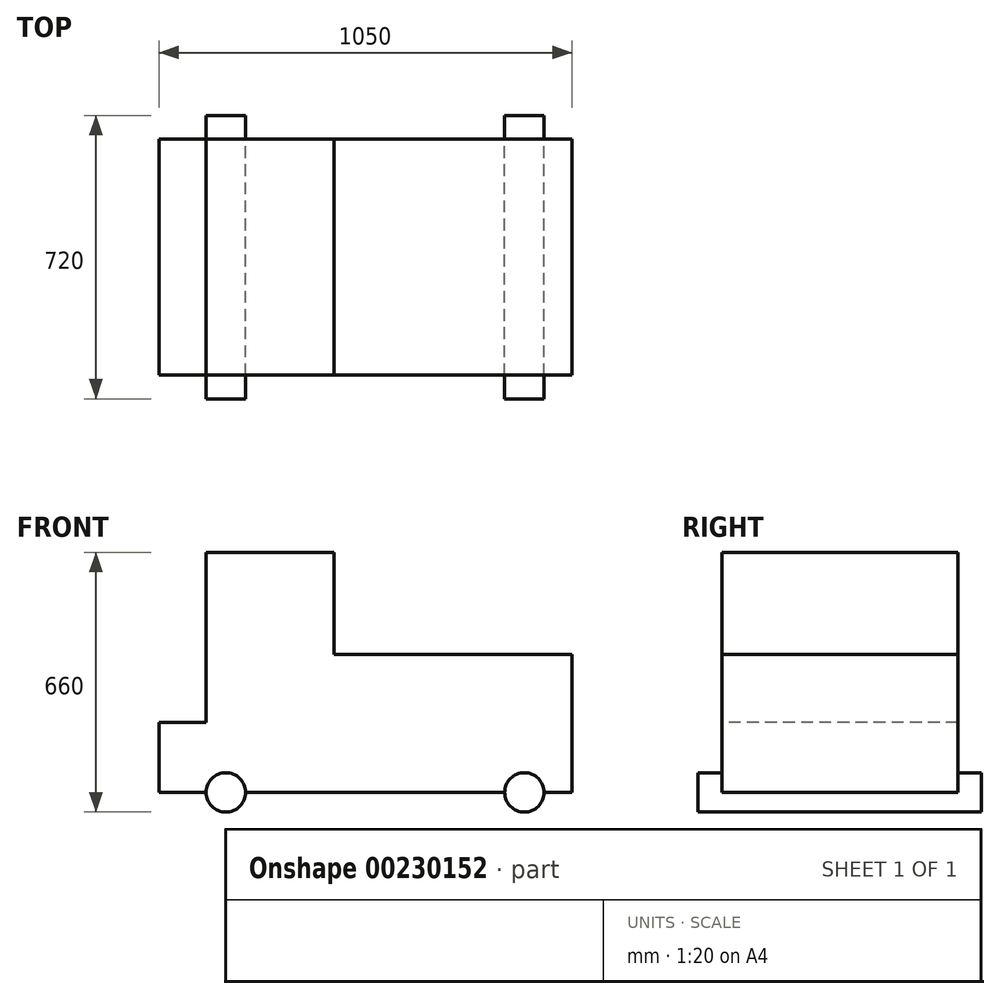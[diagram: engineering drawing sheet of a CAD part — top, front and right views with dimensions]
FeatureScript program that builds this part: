
annotation { "Feature Type Name" : "Feature", "Feature Type Description" : "" }
export const myFeature = defineFeature(function(context is Context, id is Id, definition is map)
    precondition{}
    {
        {
            var Q0;
            Q0=qCreatedBy(makeId("Top.planeOp"),FACE);
            var sketch = newSketch(context, id + "F0", { "sketchPlane" : qUnion([Q0])});
            skLineSegment(sketch, "E0.bottom", {"start": v(525, 300) * mm, "end": v(-525, 300) * mm});
            skLineSegment(sketch, "E0.top", {"start": v(525, -300) * mm, "end": v(-525, -300) * mm});
            skLineSegment(sketch, "E0.left", {"start": v(525, 300) * mm, "end": v(525, -300) * mm});
            skLineSegment(sketch, "E0.right", {"start": v(-525, 300) * mm, "end": v(-525, -300) * mm});
            skPoint(sketch, "E0.middle", {"position": v(0, 0) * mm});
            skSolve(sketch);
        }
        {
            var Q0;
            Q0 = qSketchRegion(id + "F0", true);
            extrude(context, id + "F1", {"entities" : qUnion([Q0]), "depth" : 350 * mm, "offsetDistance" : 25 * mm});
        }
        {
            var Q0;
            Q0=makeQuery(id+"F1.opExtrude","CAP_FACE",FACE,{"disambiguationData":[OSD([sQuery(id+"F0.wireOp",EDGE,"E0.bottom"),sQuery(id+"F0.wireOp",EDGE,"E0.top"),sQuery(id+"F0.wireOp",EDGE,"E0.left"),sQuery(id+"F0.wireOp",EDGE,"E0.right")])],"isStart":true});
            var sketch = newSketch(context, id + "F2", { "sketchPlane" : qUnion([Q0])});
            skLineSegment(sketch, "E1.bottom", {"start": v(-525, 300) * mm, "end": v(-80.4, 300) * mm});
            skLineSegment(sketch, "E1.top", {"start": v(-525, -300) * mm, "end": v(-80.4, -300) * mm});
            skLineSegment(sketch, "E1.left", {"start": v(-525, 300) * mm, "end": v(-525, -300) * mm});
            skLineSegment(sketch, "E1.right", {"start": v(-80.4, 300) * mm, "end": v(-80.4, -300) * mm});
            skSolve(sketch);
        }
        {
            var Q0;
            Q0 = qSketchRegion(id + "F2", true);
            extrude(context, id + "F3", {"entities" : qUnion([Q0]), "operationType" : NewBodyOperationType.ADD, "oppositeDirection" : true, "depth" : 610 * mm, "offsetDistance" : 25 * mm});
        }
        {
            var Q0;
            Q0=qCreatedBy(makeId("Front.planeOp"),FACE);
            var sketch = newSketch(context, id + "F4", { "sketchPlane" : qUnion([Q0])});
            skCircle(sketch, "E2", {"center": v(-354.83, 0) * mm, "radius": 50 * mm});
            skCircle(sketch, "E3", {"center": v(403.57, 0) * mm, "radius": 50 * mm});
            skSolve(sketch);
        }
        {
            var Q0;
            Q0 = qSketchRegion(id + "F4", true);
            extrude(context, id + "F5", {"entities" : qUnion([Q0]), "operationType" : NewBodyOperationType.ADD, "depth" : 720 * mm, "offsetDistance" : 25 * mm, "symmetric" : true});
        }
        {
            var Q0;
            Q0=makeQuery(id+"F3.boolean.opBoolean","MERGE",FACE,{"derivedFrom":[makeQuery(id+"F1.opExtrude","SWEPT_FACE",FACE,{"disambiguationData":[OSD([sQuery(id+"F0.wireOp",EDGE,"E0.right")])]}),makeQuery(id+"F3.opExtrude","SWEPT_FACE",FACE,{"disambiguationData":[OSD([sQuery(id+"F2.wireOp",EDGE,"E1.left")])]})]});
            var sketch = newSketch(context, id + "F6", { "sketchPlane" : qUnion([Q0])});
            skLineSegment(sketch, "E4.bottom", {"start": v(-300, 610) * mm, "end": v(300, 610) * mm});
            skLineSegment(sketch, "E4.top", {"start": v(-300, 177.19) * mm, "end": v(300, 177.19) * mm});
            skLineSegment(sketch, "E4.left", {"start": v(-300, 610) * mm, "end": v(-300, 177.19) * mm});
            skLineSegment(sketch, "E4.right", {"start": v(300, 610) * mm, "end": v(300, 177.19) * mm});
            skSolve(sketch);
        }
        {
            var Q0;
            Q0 = qSketchRegion(id + "F6", true);
            extrude(context, id + "F7", {"entities" : qUnion([Q0]), "operationType" : NewBodyOperationType.REMOVE, "oppositeDirection" : true, "depth" : 120 * mm, "offsetDistance" : 25 * mm});
        }
    });
